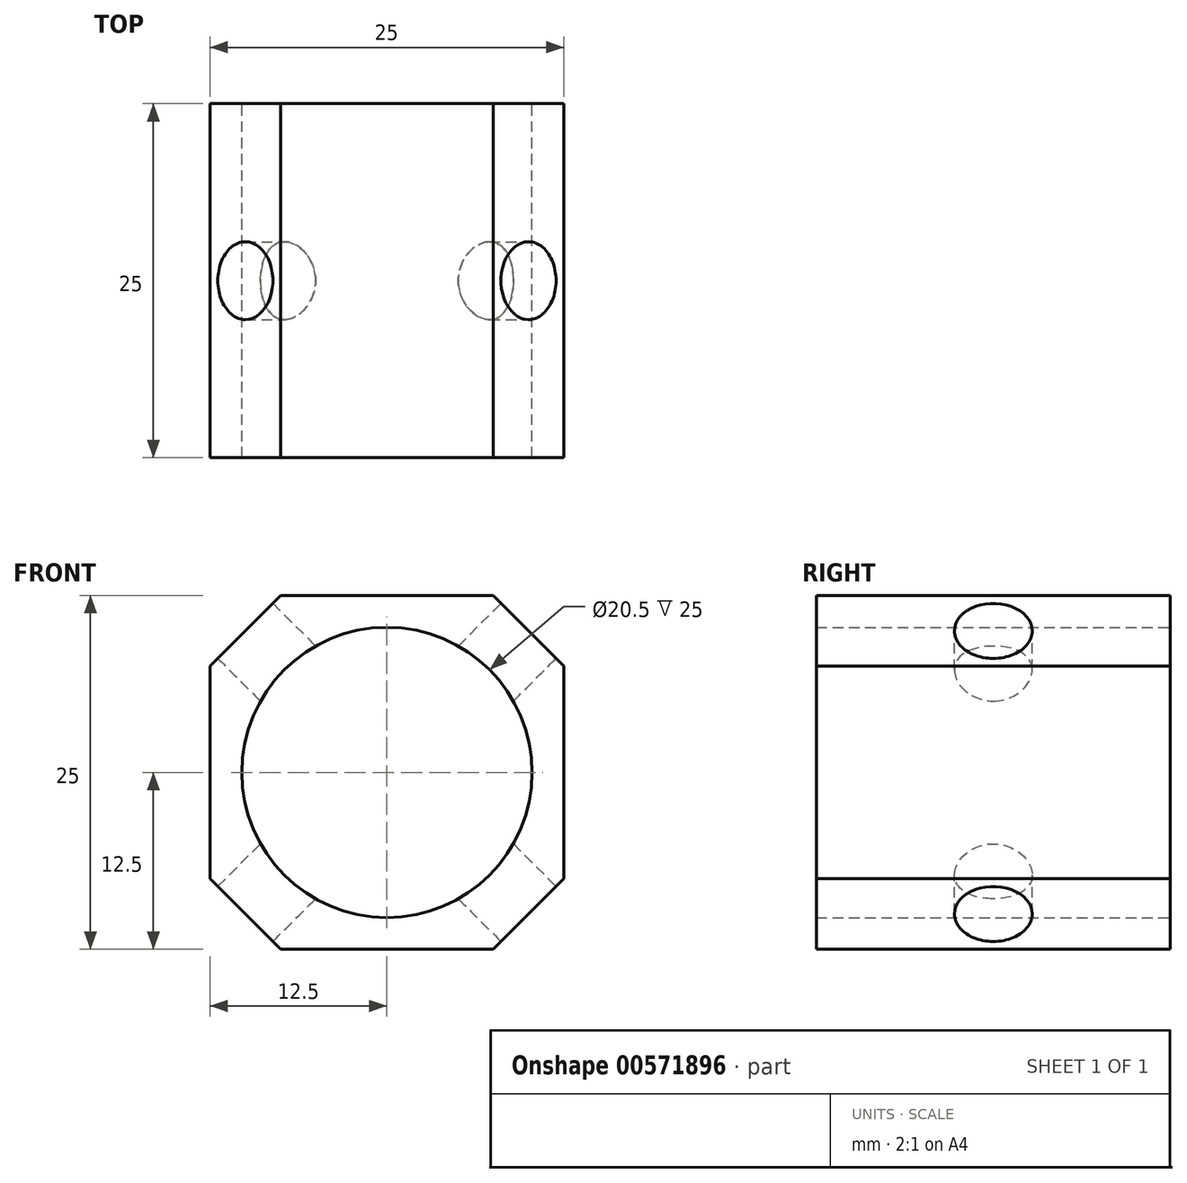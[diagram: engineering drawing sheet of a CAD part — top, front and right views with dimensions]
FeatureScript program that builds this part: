
annotation { "Feature Type Name" : "Feature", "Feature Type Description" : "" }
export const myFeature = defineFeature(function(context is Context, id is Id, definition is map)
    precondition{}
    {
        {
            var Q0;
            Q0=qCreatedBy(makeId("Front.planeOp"),FACE);
            var sketch = newSketch(context, id + "F0", { "sketchPlane" : qUnion([Q0])});
            skLineSegment(sketch, "E0.bottom", {"start": v(-12.5, -12.5) * mm, "end": v(12.5, -12.5) * mm});
            skLineSegment(sketch, "E0.top", {"start": v(-12.5, 12.5) * mm, "end": v(12.5, 12.5) * mm});
            skLineSegment(sketch, "E0.left", {"start": v(-12.5, -12.5) * mm, "end": v(-12.5, 12.5) * mm});
            skLineSegment(sketch, "E0.right", {"start": v(12.5, -12.5) * mm, "end": v(12.5, 12.5) * mm});
            skPoint(sketch, "E0.middle", {"position": v(0, 0) * mm});
            skCircle(sketch, "E1", {"center": v(0, 0) * mm, "radius": 10.25 * mm});
            skSolve(sketch);
        }
        {
            var Q0;
            Q0 = qSketchRegion(id + "F0", true);
            extrude(context, id + "F1", {"entities" : qUnion([Q0]), "depth" : 25 * mm, "offsetDistance" : 25 * mm});
        }
        {
            var Q0;
            Q0=makeQuery(id+"F1.opExtrude","SWEPT_EDGE",EDGE,{"disambiguationData":[OSD([sQuery(id+"F0.wireOp",EDGE,"E0.bottom"),sQuery(id+"F0.wireOp",EDGE,"E0.left")])]});
            var Q1;
            Q1=makeQuery(id+"F1.opExtrude","SWEPT_EDGE",EDGE,{"disambiguationData":[OSD([sQuery(id+"F0.wireOp",EDGE,"E0.bottom"),sQuery(id+"F0.wireOp",EDGE,"E0.right")])]});
            var Q2;
            Q2=makeQuery(id+"F1.opExtrude","SWEPT_EDGE",EDGE,{"disambiguationData":[OSD([sQuery(id+"F0.wireOp",EDGE,"E0.top"),sQuery(id+"F0.wireOp",EDGE,"E0.right")])]});
            var Q3;
            Q3=makeQuery(id+"F1.opExtrude","SWEPT_EDGE",EDGE,{"disambiguationData":[OSD([sQuery(id+"F0.wireOp",EDGE,"E0.top"),sQuery(id+"F0.wireOp",EDGE,"E0.left")])]});
            chamfer(context, id + "F2", {"entities" : qUnion([Q0, Q1, Q2, Q3]), "width" : 5 * mm, "tangentPropagation" : true});
        }
        {
            var Q0;
            Q0=makeQuery(id+"F2.opChamfer","BLEND_FACE",FACE,{"disambiguationData":[OSD([sQuery(id+"F0.wireOp",EDGE,"E0.top"),sQuery(id+"F0.wireOp",EDGE,"E0.right")])]});
            var sketch = newSketch(context, id + "F3", { "sketchPlane" : qUnion([Q0])});
            skCircle(sketch, "E2", {"center": v(-12.5, 0) * mm, "radius": 2.75 * mm});
            skPoint(sketch, "E2.centerSnap0", {"position": v(-12.5, -3.54) * mm});
            skSolve(sketch);
        }
        {
            var Q0;
            Q0 = qSketchRegion(id + "F3", true);
            extrude(context, id + "F4", {"entities" : qUnion([Q0]), "operationType" : NewBodyOperationType.REMOVE, "endBound" : BoundingType.THROUGH_ALL, "oppositeDirection" : true, "depth" : 25 * mm, "offsetDistance" : 25 * mm});
        }
        {
            var Q0;
            Q0=makeQuery(id+"F2.opChamfer","BLEND_FACE",FACE,{"disambiguationData":[OSD([sQuery(id+"F0.wireOp",EDGE,"E0.bottom"),sQuery(id+"F0.wireOp",EDGE,"E0.right")])]});
            var sketch = newSketch(context, id + "F5", { "sketchPlane" : qUnion([Q0])});
            skCircle(sketch, "E3", {"center": v(-12.5, 0) * mm, "radius": 2.75 * mm});
            skPoint(sketch, "E3.centerSnap0", {"position": v(-12.5, 3.54) * mm});
            skSolve(sketch);
        }
        {
            var Q0;
            Q0 = qSketchRegion(id + "F5", true);
            extrude(context, id + "F6", {"entities" : qUnion([Q0]), "operationType" : NewBodyOperationType.REMOVE, "endBound" : BoundingType.THROUGH_ALL, "oppositeDirection" : true, "depth" : 25 * mm, "offsetDistance" : 25 * mm});
        }
    });
